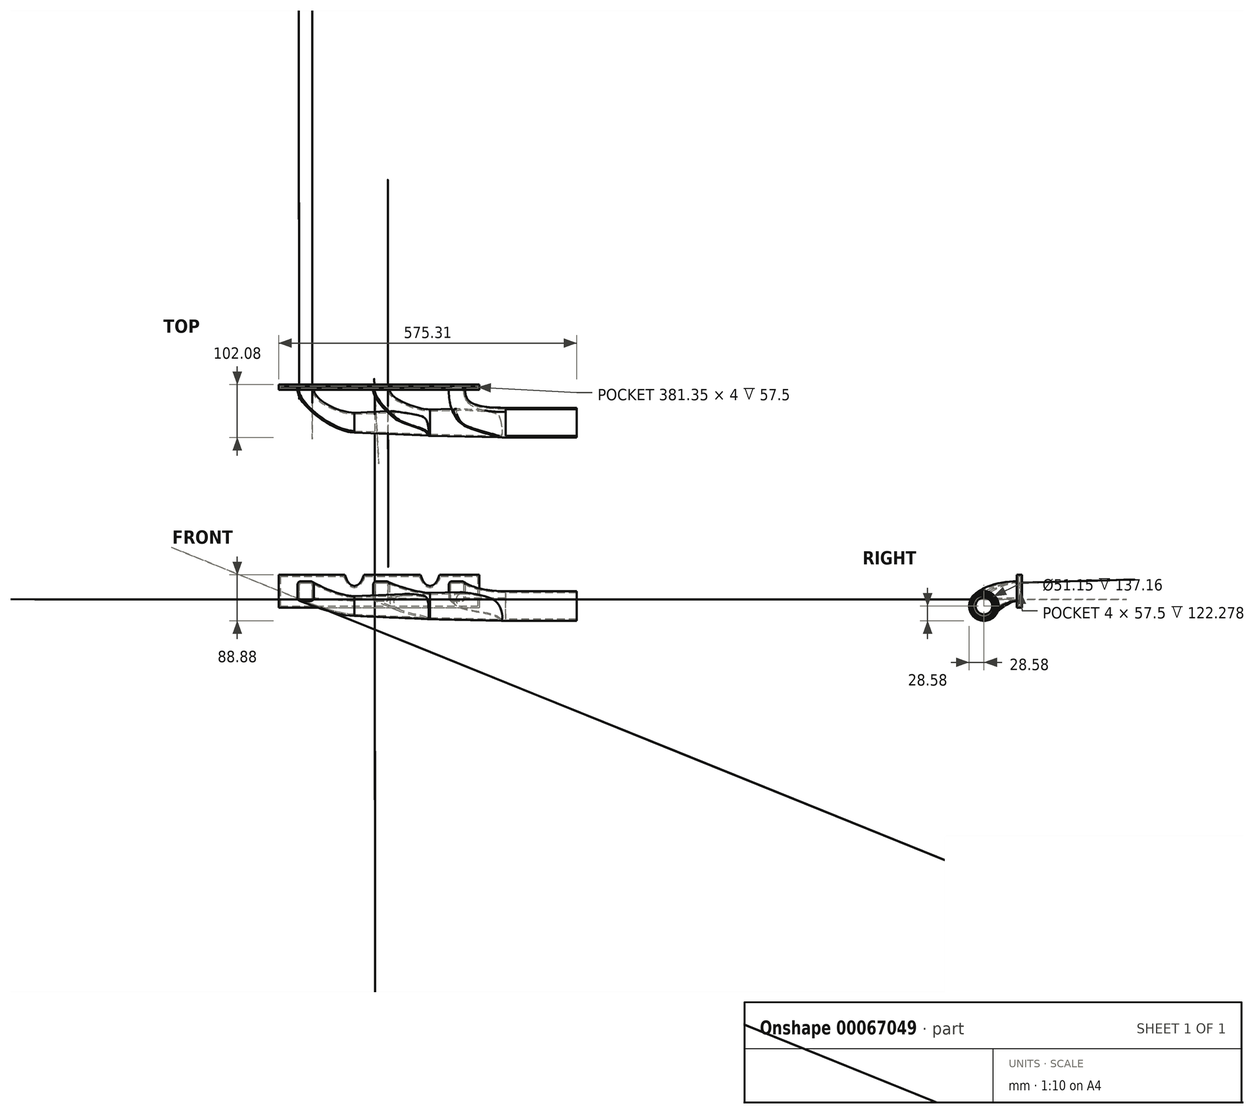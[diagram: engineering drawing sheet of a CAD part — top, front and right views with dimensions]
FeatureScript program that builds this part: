
annotation { "Feature Type Name" : "Feature", "Feature Type Description" : "" }
export const myFeature = defineFeature(function(context is Context, id is Id, definition is map)
    precondition{}
    {
        {
            var Q0;
            Q0=qCreatedBy(makeId("Front.planeOp"),FACE);
            var sketch = newSketch(context, id + "F0", { "sketchPlane" : qUnion([Q0])});
            skLineSegment(sketch, "E0.bottom", {"start": v(-146.05, 0) * mm, "end": v(-18.63, 0) * mm});
            skLineSegment(sketch, "E0.left", {"start": v(-146.05, 0) * mm, "end": v(-146.05, -63.5) * mm});
            skLineSegment(sketch, "E0.right", {"start": v(241.3, 0) * mm, "end": v(241.3, -63.5) * mm});
            skLineSegment(sketch, "E1", {"start": v(-146.05, -31.75) * mm, "end": v(241.3, -31.75) * mm, "construction": true});
            skEllipticalArc(sketch, "E2.MirrorCS", {});
            skEllipticalArc(sketch, "E3.MirrorCS", {});
            skLineSegment(sketch, "E4", {"start": v(-146.05, -63.5) * mm, "end": v(241.3, -63.5) * mm});
            skLineSegment(sketch, "E5.trimOffspring", {"start": v(18.63, 0) * mm, "end": v(127.42, 0) * mm});
            skLineSegment(sketch, "E6.trimOffspring", {"start": v(164.68, 0) * mm, "end": v(241.3, 0) * mm});
            const initialGuessF0  = {"E2.MirrorCS": [0, 0.03568, 0, -1, 0.05734, 0.023805, 5.3840067622967815, 0.8991785448828047], "E3.MirrorCS": [0.14605, 0.03568, 0, -1, 0.05734, 0.023805, 5.3840067622967815, 0.8991785448828047]};
            skSetInitialGuess(sketch, initialGuessF0);
            skSolve(sketch);
        }
        {
            var Q0;
            Q0=qCreatedBy(makeId("Right.planeOp"),FACE);
            cPlane(context, id + "F1", {"entities" : qUnion([Q0]), "cplaneType" : CPlaneType.OFFSET, "offset" : 146.05 * mm, "width" : 152.4 * mm, "height" : 152.4 * mm});
        }
        {
            var Q0;
            Q0=qCreatedBy(id+"F1.planeOp",FACE);
            cPlane(context, id + "F2", {"entities" : qUnion([Q0]), "cplaneType" : CPlaneType.OFFSET, "offset" : 146.05 * mm, "width" : 152.4 * mm, "height" : 152.4 * mm});
        }
        {
            var Q0;
            Q0=qCreatedBy(makeId("Front.planeOp"),FACE);
            var sketch = newSketch(context, id + "F3", { "sketchPlane" : qUnion([Q0])});
            skLineSegment(sketch, "E7.rect.bottom", {"start": v(-103.5, -12.7) * mm, "end": v(-84.45, -12.7) * mm});
            skArc(sketch, "E8.filletArc", {"start": v(-78.1, -19.05) * mm, "mid": v(-79.96, -14.56) * mm, "end": v(-84.45, -12.7) * mm});
            skLineSegment(sketch, "E7.rect.right", {"start": v(-78.1, -19.05) * mm, "end": v(-78.1, -44.45) * mm});
            skArc(sketch, "E9.filletArc", {"start": v(-84.45, -50.8) * mm, "mid": v(-79.96, -48.94) * mm, "end": v(-78.1, -44.45) * mm});
            skLineSegment(sketch, "E7.rect.top", {"start": v(-103.5, -50.8) * mm, "end": v(-84.45, -50.8) * mm});
            skArc(sketch, "E10.filletArc", {"start": v(-109.86, -44.45) * mm, "mid": v(-108, -48.94) * mm, "end": v(-103.5, -50.8) * mm});
            skLineSegment(sketch, "E7.rect.left", {"start": v(-109.86, -19.05) * mm, "end": v(-109.86, -44.45) * mm});
            skArc(sketch, "E11.filletArc", {"start": v(-103.5, -12.7) * mm, "mid": v(-108, -14.56) * mm, "end": v(-109.86, -19.05) * mm});
            skLineSegment(sketch, "E12", {"start": v(-137.86, -31.75) * mm, "end": v(-109.86, -31.75) * mm, "construction": true});
            skPoint(sketch, "E12.startSnap0", {"position": v(-109.86, -31.75) * mm});
            skSolve(sketch);
        }
        {
            var Q0;
            Q0=qCreatedBy(makeId("Front.planeOp"),FACE);
            var sketch = newSketch(context, id + "F4", { "sketchPlane" : qUnion([Q0])});
            skLineSegment(sketch, "E13.rect.bottom", {"start": v(42.55, -12.7) * mm, "end": v(61.6, -12.7) * mm});
            skArc(sketch, "E14.filletArc", {"start": v(67.95, -19.05) * mm, "mid": v(66.09, -14.56) * mm, "end": v(61.6, -12.7) * mm});
            skLineSegment(sketch, "E13.rect.right", {"start": v(67.95, -19.05) * mm, "end": v(67.95, -44.45) * mm});
            skArc(sketch, "E15.filletArc", {"start": v(61.6, -50.8) * mm, "mid": v(66.09, -48.94) * mm, "end": v(67.95, -44.45) * mm});
            skLineSegment(sketch, "E13.rect.top", {"start": v(42.55, -50.8) * mm, "end": v(61.6, -50.8) * mm});
            skArc(sketch, "E16.filletArc", {"start": v(36.2, -44.45) * mm, "mid": v(38.05, -48.94) * mm, "end": v(42.55, -50.8) * mm});
            skLineSegment(sketch, "E13.rect.left", {"start": v(36.2, -19.05) * mm, "end": v(36.2, -44.45) * mm});
            skArc(sketch, "E17.filletArc", {"start": v(42.55, -12.7) * mm, "mid": v(38.05, -14.56) * mm, "end": v(36.2, -19.05) * mm});
            skLineSegment(sketch, "E18", {"start": v(36.2, -31.75) * mm, "end": v(-146.05, -31.75) * mm, "construction": true});
            skSolve(sketch);
        }
        {
            var Q0;
            Q0=qCreatedBy(makeId("Front.planeOp"),FACE);
            var sketch = newSketch(context, id + "F5", { "sketchPlane" : qUnion([Q0])});
            skLineSegment(sketch, "E19.rect.bottom", {"start": v(188.6, -12.7) * mm, "end": v(207.65, -12.7) * mm});
            skArc(sketch, "E20.filletArc", {"start": v(214, -19.05) * mm, "mid": v(212.14, -14.56) * mm, "end": v(207.65, -12.7) * mm});
            skLineSegment(sketch, "E19.rect.right", {"start": v(214, -19.05) * mm, "end": v(214, -44.45) * mm});
            skArc(sketch, "E21.filletArc", {"start": v(207.65, -50.8) * mm, "mid": v(212.14, -48.94) * mm, "end": v(214, -44.45) * mm});
            skLineSegment(sketch, "E19.rect.top", {"start": v(188.6, -50.8) * mm, "end": v(207.65, -50.8) * mm});
            skArc(sketch, "E22.filletArc", {"start": v(182.25, -44.45) * mm, "mid": v(184.1, -48.94) * mm, "end": v(188.6, -50.8) * mm});
            skLineSegment(sketch, "E19.rect.left", {"start": v(182.25, -19.05) * mm, "end": v(182.25, -44.45) * mm});
            skArc(sketch, "E23.filletArc", {"start": v(188.6, -12.7) * mm, "mid": v(184.1, -14.56) * mm, "end": v(182.25, -19.05) * mm});
            skLineSegment(sketch, "E24", {"start": v(182.25, -31.75) * mm, "end": v(-146.05, -31.75) * mm, "construction": true});
            skSolve(sketch);
        }
        {
            var Q0;
            Q0=qCreatedBy(makeId("Right.planeOp"),FACE);
            var sketch = newSketch(context, id + "F6", { "sketchPlane" : qUnion([Q0])});
            skCircle(sketch, "E25", {"center": v(-63.5, -60.3) * mm, "radius": 19.05 * mm});
            skSolve(sketch);
        }
        {
            var Q0;
            Q0=qCreatedBy(id+"F2.planeOp",FACE);
            var sketch = newSketch(context, id + "F7", { "sketchPlane" : qUnion([Q0])});
            skCircle(sketch, "E26", {"center": v(-63.5, -60.3) * mm, "radius": 28.57 * mm});
            skSolve(sketch);
        }
        {
            var Q0;
            Q0=qCreatedBy(id+"F1.planeOp",FACE);
            var sketch = newSketch(context, id + "F8", { "sketchPlane" : qUnion([Q0])});
            skCircle(sketch, "E27", {"center": v(-63.5, -60.3) * mm, "radius": 25.4 * mm});
            skSolve(sketch);
        }
        {
            var Q0;
            Q0=makeQuery(id+"F6.imprint","IMPRINT",FACE,{"disambiguationData":[TD([[makeQuery(id+"F6.imprint","IMPRINT",EDGE,{"derivedFrom":sQuery(id+"F6.wireOp",EDGE,"E25")}),1.0]])]});
            var Q1;
            Q1=makeQuery(id+"F8.imprint","IMPRINT",FACE,{"disambiguationData":[TD([[makeQuery(id+"F8.imprint","IMPRINT",EDGE,{"derivedFrom":sQuery(id+"F8.wireOp",EDGE,"E27")}),1.0]])]});
            loft(context, id + "F9", {"sheetProfilesArray" : [{ "sheetProfileEntities" : qUnion([Q0]) }, { "sheetProfileEntities" : qUnion([Q1]) }]});
        }
        {
            var Q1;
            Q1=qSketchRegion(id+"F7",true);
            var Q2;
            Q2=qSketchRegion(id+"F8",true);
            loft(context, id + "F10", {"operationType" : NewBodyOperationType.ADD, "sheetProfilesArray" : [{ "sheetProfileEntities" : qUnion([Q1]) }, { "sheetProfileEntities" : qUnion([Q2]) }]});
        }
        {
            var Q1;
            Q1=qSketchRegion(id+"F6",true);
            var Q2;
            Q2=qSketchRegion(id+"F3",true);
            loft(context, id + "F11", {"operationType" : NewBodyOperationType.ADD, "startCondition" : LoftEndDerivativeType.NORMAL_TO_PROFILE, "startMagnitude" : 1.1, "endCondition" : LoftEndDerivativeType.NORMAL_TO_PROFILE, "endMagnitude" : 1.1, "sheetProfilesArray" : [{ "sheetProfileEntities" : qUnion([Q1]) }, { "sheetProfileEntities" : qUnion([Q2]) }]});
        }
        {
            var Q1;
            Q1=qSketchRegion(id+"F7",true);
            var Q2;
            Q2=qSketchRegion(id+"F5",true);
            loft(context, id + "F12", {"operationType" : NewBodyOperationType.ADD, "startCondition" : LoftEndDerivativeType.NORMAL_TO_PROFILE, "startMagnitude" : 2, "endCondition" : LoftEndDerivativeType.NORMAL_TO_PROFILE, "endMagnitude" : 2, "sheetProfilesArray" : [{ "sheetProfileEntities" : qUnion([Q1]) }, { "sheetProfileEntities" : qUnion([Q2]) }]});
        }
        {
            var Q1;
            Q1=qSketchRegion(id+"F8",true);
            var Q2;
            Q2=qSketchRegion(id+"F4",true);
            loft(context, id + "F13", {"operationType" : NewBodyOperationType.ADD, "startCondition" : LoftEndDerivativeType.NORMAL_TO_PROFILE, "startMagnitude" : 1, "endCondition" : LoftEndDerivativeType.NORMAL_TO_PROFILE, "endMagnitude" : 1, "sheetProfilesArray" : [{ "sheetProfileEntities" : qUnion([Q1]) }, { "sheetProfileEntities" : qUnion([Q2]) }]});
        }
        {
            var Q0;
            Q0=qSketchRegion(id+"F0",true);
            extrude(context, id + "F14", {"entities" : qUnion([Q0]), "operationType" : NewBodyOperationType.ADD, "oppositeDirection" : true, "depth" : 10 * mm});
        }
        {
            var Q0;
            Q0=makeQuery(id+"F7.imprint","IMPRINT",FACE,{"disambiguationData":[TD([[makeQuery(id+"F7.imprint","IMPRINT",EDGE,{"derivedFrom":sQuery(id+"F7.wireOp",EDGE,"E26")}),1.0]])]});
            var sketch = newSketch(context, id + "F15", { "sketchPlane" : qUnion([Q0])});
            skCircle(sketch, "E28", {"center": v(-63.5, -60.3) * mm, "radius": 28.57 * mm});
            skSolve(sketch);
        }
        {
            var Q0;
            Q0=qSketchRegion(id+"F15",true);
            extrude(context, id + "F16", {"entities" : qUnion([Q0]), "operationType" : NewBodyOperationType.ADD, "depth" : 137.16 * mm});
        }
        {
            var Q0;
            Q0=makeQuery(id+"F16.opExtrude","CAP_FACE",FACE,{"disambiguationData":[OSD([sQuery(id+"F15.wireOp",EDGE,"E28")])],"isStart":false});
            var Q1;
            Q1=makeQuery(id+"F16.opExtrude","CAP_FACE",FACE,{"disambiguationData":[OSD([sQuery(id+"F15.wireOp",EDGE,"E28")])],"isStart":false});
            shell(context, id + "F17", {"entities" : qUnion([Q0, Q1]), "thickness" : 3 * mm});
        }
    });
